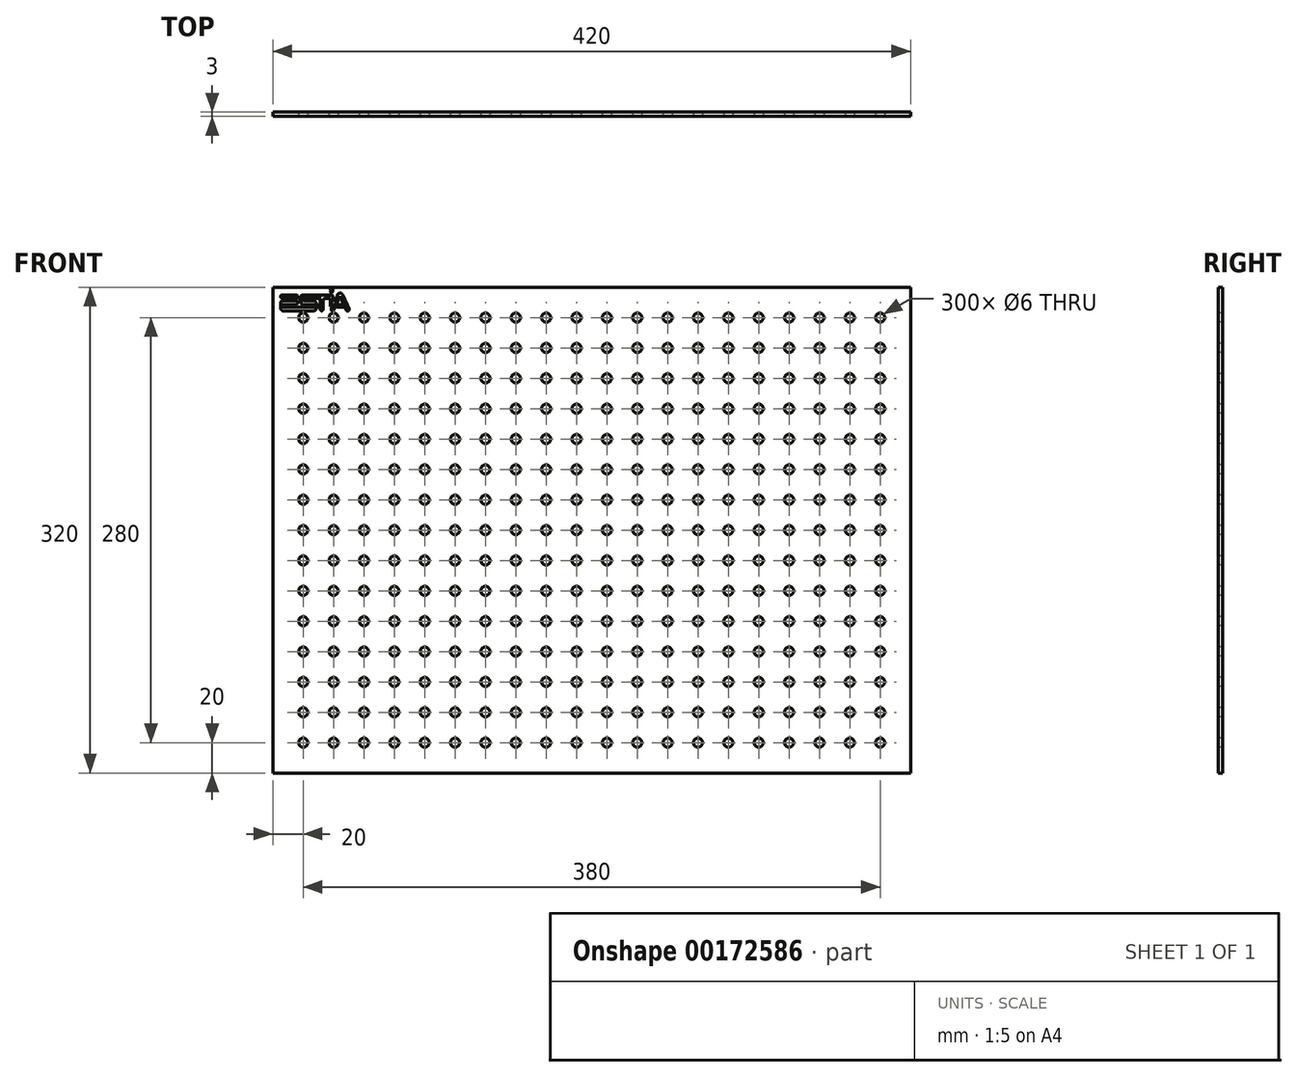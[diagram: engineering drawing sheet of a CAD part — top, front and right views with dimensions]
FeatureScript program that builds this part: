
annotation { "Feature Type Name" : "Feature", "Feature Type Description" : "" }
export const myFeature = defineFeature(function(context is Context, id is Id, definition is map)
    precondition{}
    {
        {
            var Q0;
            Q0=qCreatedBy(makeId("Front.planeOp"),FACE);
            var sketch = newSketch(context, id + "F0", { "sketchPlane" : qUnion([Q0])});
            skLineSegment(sketch, "E0.bottom", {"start": v(0, 0) * mm, "end": v(420, 0) * mm});
            skLineSegment(sketch, "E0.top", {"start": v(0, 320) * mm, "end": v(420, 320) * mm});
            skLineSegment(sketch, "E0.left", {"start": v(0, 0) * mm, "end": v(0, 320) * mm});
            skLineSegment(sketch, "E0.right", {"start": v(420, 0) * mm, "end": v(420, 320) * mm});
            skSolve(sketch);
        }
        {
            var Q0;
            Q0 = qSketchRegion(id + "F0", true);
            extrude(context, id + "F1", {"entities" : qUnion([Q0]), "depth" : 3 * mm});
        }
        {
            var Q0;
            Q0=makeQuery(id+"F1.opExtrude","CAP_FACE",FACE,{"disambiguationData":[OSD([sQuery(id+"F0.wireOp",EDGE,"E0.bottom"),sQuery(id+"F0.wireOp",EDGE,"E0.top"),sQuery(id+"F0.wireOp",EDGE,"E0.left"),sQuery(id+"F0.wireOp",EDGE,"E0.right")])],"isStart":false});
            var sketch = newSketch(context, id + "F2", { "sketchPlane" : qUnion([Q0])});
            skLineSegment(sketch, "E1.0.0", {"start": v(6.34, 307.22) * mm, "end": v(6.34, 308.64) * mm});
            skLineSegment(sketch, "E1.0.1", {"start": v(6.34, 308.64) * mm, "end": v(15.34, 308.64) * mm});
            skLineSegment(sketch, "E1.0.38", {"start": v(15.34, 310.92) * mm, "end": v(6.2, 310.92) * mm});
            skLineSegment(sketch, "E1.0.57", {"start": v(5, 309.72) * mm, "end": v(5, 306.79) * mm});
            skArc(sketch, "E1.0.59", {"start": v(5, 306.79) * mm, "mid": v(5.36, 305.44) * mm, "end": v(6.34, 304.45) * mm});
            skLineSegment(sketch, "E1.0.60", {"start": v(6.34, 304.45) * mm, "end": v(27.4, 304.45) * mm});
            skArc(sketch, "E1.0.61", {"start": v(27.4, 304.45) * mm, "mid": v(29.2, 307.64) * mm, "end": v(27.56, 310.92) * mm});
            skLineSegment(sketch, "E1.0.62", {"start": v(27.56, 310.92) * mm, "end": v(19.38, 310.92) * mm});
            skArc(sketch, "E1.0.63", {"start": v(19.38, 310.92) * mm, "mid": v(19.06, 311.83) * mm, "end": v(19.4, 312.71) * mm});
            skLineSegment(sketch, "E1.0.64", {"start": v(19.4, 312.71) * mm, "end": v(31.79, 312.71) * mm});
            skArc(sketch, "E1.0.65", {"start": v(31.79, 312.71) * mm, "mid": v(31.41, 311.84) * mm, "end": v(31.29, 310.9) * mm});
            skLineSegment(sketch, "E1.0.66", {"start": v(31.29, 310.9) * mm, "end": v(31.29, 305.3) * mm});
            skArc(sketch, "E1.0.67", {"start": v(31.29, 305.3) * mm, "mid": v(32.15, 304.44) * mm, "end": v(33.01, 305.3) * mm});
            skLineSegment(sketch, "E1.0.68", {"start": v(33.01, 305.3) * mm, "end": v(33.01, 310.9) * mm});
            skArc(sketch, "E1.0.69", {"start": v(33.01, 310.9) * mm, "mid": v(33.54, 312.18) * mm, "end": v(34.82, 312.71) * mm});
            skLineSegment(sketch, "E1.0.70", {"start": v(34.82, 312.71) * mm, "end": v(37.81, 312.71) * mm});
            skLineSegment(sketch, "E1.0.71", {"start": v(37.81, 312.71) * mm, "end": v(37.81, 308.44) * mm});
            skArc(sketch, "E1.0.72", {"start": v(37.81, 308.44) * mm, "mid": v(37.92, 307.8) * mm, "end": v(38.22, 307.23) * mm});
            skLineSegment(sketch, "E1.0.73", {"start": v(38.22, 307.23) * mm, "end": v(39.53, 310.23) * mm});
            skLineSegment(sketch, "E1.0.74", {"start": v(39.53, 310.23) * mm, "end": v(39.53, 314.05) * mm});
            skArc(sketch, "E1.0.75", {"start": v(39.53, 314.05) * mm, "mid": v(39.25, 314.72) * mm, "end": v(38.58, 315) * mm});
            skLineSegment(sketch, "E1.0.76", {"start": v(38.58, 315) * mm, "end": v(19.43, 315) * mm});
            skArc(sketch, "E1.0.77", {"start": v(19.43, 315) * mm, "mid": v(17.77, 311.83) * mm, "end": v(19.38, 308.64) * mm});
            skLineSegment(sketch, "E1.0.78", {"start": v(19.38, 308.64) * mm, "end": v(27.56, 308.64) * mm});
            skArc(sketch, "E1.0.79", {"start": v(27.56, 308.64) * mm, "mid": v(28, 307.74) * mm, "end": v(27.56, 306.84) * mm});
            skLineSegment(sketch, "E1.0.80", {"start": v(27.56, 306.84) * mm, "end": v(6.72, 306.84) * mm});
            skArc(sketch, "E1.0.81", {"start": v(6.72, 306.84) * mm, "mid": v(6.45, 306.95) * mm, "end": v(6.34, 307.22) * mm});
            skLineSegment(sketch, "E2.0.2", {"start": v(6.2, 312.71) * mm, "end": v(15.34, 312.71) * mm});
            skLineSegment(sketch, "E2.0.39", {"start": v(15.34, 315) * mm, "end": v(6.2, 315) * mm});
            skLineSegment(sketch, "E3.0.0", {"start": v(44.28, 314.22) * mm, "end": v(48.34, 304.91) * mm});
            skArc(sketch, "E3.0.1", {"start": v(48.34, 304.91) * mm, "mid": v(49.63, 304.4) * mm, "end": v(50.13, 305.7) * mm});
            skLineSegment(sketch, "E3.0.2", {"start": v(50.13, 305.7) * mm, "end": v(46.06, 315) * mm});
            skArc(sketch, "E3.0.3", {"start": v(46.06, 315) * mm, "mid": v(44.28, 316.17) * mm, "end": v(42.49, 315) * mm});
            skLineSegment(sketch, "E3.0.4", {"start": v(42.49, 315) * mm, "end": v(38.42, 305.7) * mm});
            skArc(sketch, "E3.0.5", {"start": v(38.42, 305.7) * mm, "mid": v(38.92, 304.4) * mm, "end": v(40.2, 304.91) * mm});
            skLineSegment(sketch, "E3.0.6", {"start": v(40.2, 304.91) * mm, "end": v(44.28, 314.22) * mm});
            skLineSegment(sketch, "E4.0.2", {"start": v(42.78, 306.84) * mm, "end": v(45.78, 306.84) * mm});
            skLineSegment(sketch, "E4.0.39", {"start": v(45.78, 308.64) * mm, "end": v(42.78, 308.64) * mm});
            skLineSegment(sketch, "E5", {"start": v(32.15, 305.3) * mm, "end": v(49.24, 305.3) * mm, "construction": true});
            skLineSegment(sketch, "E6", {"start": v(26.84, 307.74) * mm, "end": v(8.07, 307.74) * mm, "construction": true});
            skLineSegment(sketch, "E7", {"start": v(7.84, 311.8) * mm, "end": v(20.44, 311.8) * mm, "construction": true});
            skArc(sketch, "E8", {"start": v(6.2, 315) * mm, "mid": v(5.06, 313.86) * mm, "end": v(6.2, 312.71) * mm});
            skArc(sketch, "E9", {"start": v(15.34, 312.71) * mm, "mid": v(16.48, 313.86) * mm, "end": v(15.34, 315) * mm});
            skArc(sketch, "E10", {"start": v(15.34, 308.64) * mm, "mid": v(16.48, 309.78) * mm, "end": v(15.34, 310.92) * mm});
            skArc(sketch, "E11", {"start": v(6.2, 310.92) * mm, "mid": v(5.35, 310.57) * mm, "end": v(5, 309.72) * mm});
            skArc(sketch, "E12", {"start": v(45.78, 306.84) * mm, "mid": v(46.67, 307.74) * mm, "end": v(45.78, 308.64) * mm});
            skArc(sketch, "E13", {"start": v(42.78, 308.64) * mm, "mid": v(41.88, 307.74) * mm, "end": v(42.78, 306.84) * mm});
            skLineSegment(sketch, "E14", {"start": v(42.78, 307.74) * mm, "end": v(45.78, 307.74) * mm, "construction": true});
            skLineSegment(sketch, "E15", {"start": v(44.28, 301.39) * mm, "end": v(44.28, 307.74) * mm, "construction": true});
            skEllipse(sketch, "E16", {"center": v(38.58, 317.9) * mm, "majorRadius": 1.33 * mm, "minorRadius": 0.9 * mm, "majorAxis": v(0, 1)});
            skLineSegment(sketch, "E17", {"start": v(38.58, 310.9) * mm, "end": v(38.58, 315) * mm, "construction": true});
            skSolve(sketch);
        }
        {
            var Q0;
            Q0=makeQuery(id+"F1.opExtrude","CAP_FACE",FACE,{"disambiguationData":[OSD([sQuery(id+"F0.wireOp",EDGE,"E0.bottom"),sQuery(id+"F0.wireOp",EDGE,"E0.top"),sQuery(id+"F0.wireOp",EDGE,"E0.left"),sQuery(id+"F0.wireOp",EDGE,"E0.right")])],"isStart":false});
            var sketch = newSketch(context, id + "F3", { "sketchPlane" : qUnion([Q0])});
            skCircle(sketch, "E18", {"center": v(20, 300) * mm, "radius": 3 * mm});
            skCircle(sketch, "E19.0.1.0", {"center": v(20, 280) * mm, "radius": 3 * mm});
            skCircle(sketch, "E19.0.2.0", {"center": v(20, 260) * mm, "radius": 3 * mm});
            skCircle(sketch, "E19.0.3.0", {"center": v(20, 240) * mm, "radius": 3 * mm});
            skCircle(sketch, "E19.0.4.0", {"center": v(20, 220) * mm, "radius": 3 * mm});
            skCircle(sketch, "E19.0.5.0", {"center": v(20, 200) * mm, "radius": 3 * mm});
            skCircle(sketch, "E19.0.6.0", {"center": v(20, 180) * mm, "radius": 3 * mm});
            skCircle(sketch, "E19.0.7.0", {"center": v(20, 160) * mm, "radius": 3 * mm});
            skCircle(sketch, "E19.0.8.0", {"center": v(20, 140) * mm, "radius": 3 * mm});
            skCircle(sketch, "E19.0.9.0", {"center": v(20, 120) * mm, "radius": 3 * mm});
            skCircle(sketch, "E19.0.10.0", {"center": v(20, 100) * mm, "radius": 3 * mm});
            skCircle(sketch, "E19.0.11.0", {"center": v(20, 80) * mm, "radius": 3 * mm});
            skCircle(sketch, "E19.0.12.0", {"center": v(20, 60) * mm, "radius": 3 * mm});
            skCircle(sketch, "E19.0.13.0", {"center": v(20, 40) * mm, "radius": 3 * mm});
            skCircle(sketch, "E19.0.14.0", {"center": v(20, 20) * mm, "radius": 3 * mm});
            skCircle(sketch, "E19.1.0.0", {"center": v(40, 300) * mm, "radius": 3 * mm});
            skCircle(sketch, "E19.1.1.0", {"center": v(40, 280) * mm, "radius": 3 * mm});
            skCircle(sketch, "E19.1.2.0", {"center": v(40, 260) * mm, "radius": 3 * mm});
            skCircle(sketch, "E19.1.3.0", {"center": v(40, 240) * mm, "radius": 3 * mm});
            skCircle(sketch, "E19.1.4.0", {"center": v(40, 220) * mm, "radius": 3 * mm});
            skCircle(sketch, "E19.1.5.0", {"center": v(40, 200) * mm, "radius": 3 * mm});
            skCircle(sketch, "E19.1.6.0", {"center": v(40, 180) * mm, "radius": 3 * mm});
            skCircle(sketch, "E19.1.7.0", {"center": v(40, 160) * mm, "radius": 3 * mm});
            skCircle(sketch, "E19.1.8.0", {"center": v(40, 140) * mm, "radius": 3 * mm});
            skCircle(sketch, "E19.1.9.0", {"center": v(40, 120) * mm, "radius": 3 * mm});
            skCircle(sketch, "E19.1.10.0", {"center": v(40, 100) * mm, "radius": 3 * mm});
            skCircle(sketch, "E19.1.11.0", {"center": v(40, 80) * mm, "radius": 3 * mm});
            skCircle(sketch, "E19.1.12.0", {"center": v(40, 60) * mm, "radius": 3 * mm});
            skCircle(sketch, "E19.1.13.0", {"center": v(40, 40) * mm, "radius": 3 * mm});
            skCircle(sketch, "E19.1.14.0", {"center": v(40, 20) * mm, "radius": 3 * mm});
            skCircle(sketch, "E19.2.0.0", {"center": v(60, 300) * mm, "radius": 3 * mm});
            skCircle(sketch, "E19.2.1.0", {"center": v(60, 280) * mm, "radius": 3 * mm});
            skCircle(sketch, "E19.2.2.0", {"center": v(60, 260) * mm, "radius": 3 * mm});
            skCircle(sketch, "E19.2.3.0", {"center": v(60, 240) * mm, "radius": 3 * mm});
            skCircle(sketch, "E19.2.4.0", {"center": v(60, 220) * mm, "radius": 3 * mm});
            skCircle(sketch, "E19.2.5.0", {"center": v(60, 200) * mm, "radius": 3 * mm});
            skCircle(sketch, "E19.2.6.0", {"center": v(60, 180) * mm, "radius": 3 * mm});
            skCircle(sketch, "E19.2.7.0", {"center": v(60, 160) * mm, "radius": 3 * mm});
            skCircle(sketch, "E19.2.8.0", {"center": v(60, 140) * mm, "radius": 3 * mm});
            skCircle(sketch, "E19.2.9.0", {"center": v(60, 120) * mm, "radius": 3 * mm});
            skCircle(sketch, "E19.2.10.0", {"center": v(60, 100) * mm, "radius": 3 * mm});
            skCircle(sketch, "E19.2.11.0", {"center": v(60, 80) * mm, "radius": 3 * mm});
            skCircle(sketch, "E19.2.12.0", {"center": v(60, 60) * mm, "radius": 3 * mm});
            skCircle(sketch, "E19.2.13.0", {"center": v(60, 40) * mm, "radius": 3 * mm});
            skCircle(sketch, "E19.2.14.0", {"center": v(60, 20) * mm, "radius": 3 * mm});
            skCircle(sketch, "E19.3.0.0", {"center": v(80, 300) * mm, "radius": 3 * mm});
            skCircle(sketch, "E19.3.1.0", {"center": v(80, 280) * mm, "radius": 3 * mm});
            skCircle(sketch, "E19.3.2.0", {"center": v(80, 260) * mm, "radius": 3 * mm});
            skCircle(sketch, "E19.3.3.0", {"center": v(80, 240) * mm, "radius": 3 * mm});
            skCircle(sketch, "E19.3.4.0", {"center": v(80, 220) * mm, "radius": 3 * mm});
            skCircle(sketch, "E19.3.5.0", {"center": v(80, 200) * mm, "radius": 3 * mm});
            skCircle(sketch, "E19.3.6.0", {"center": v(80, 180) * mm, "radius": 3 * mm});
            skCircle(sketch, "E19.3.7.0", {"center": v(80, 160) * mm, "radius": 3 * mm});
            skCircle(sketch, "E19.3.8.0", {"center": v(80, 140) * mm, "radius": 3 * mm});
            skCircle(sketch, "E19.3.9.0", {"center": v(80, 120) * mm, "radius": 3 * mm});
            skCircle(sketch, "E19.3.10.0", {"center": v(80, 100) * mm, "radius": 3 * mm});
            skCircle(sketch, "E19.3.11.0", {"center": v(80, 80) * mm, "radius": 3 * mm});
            skCircle(sketch, "E19.3.12.0", {"center": v(80, 60) * mm, "radius": 3 * mm});
            skCircle(sketch, "E19.3.13.0", {"center": v(80, 40) * mm, "radius": 3 * mm});
            skCircle(sketch, "E19.3.14.0", {"center": v(80, 20) * mm, "radius": 3 * mm});
            skCircle(sketch, "E19.4.0.0", {"center": v(100, 300) * mm, "radius": 3 * mm});
            skCircle(sketch, "E19.4.1.0", {"center": v(100, 280) * mm, "radius": 3 * mm});
            skCircle(sketch, "E19.4.2.0", {"center": v(100, 260) * mm, "radius": 3 * mm});
            skCircle(sketch, "E19.4.3.0", {"center": v(100, 240) * mm, "radius": 3 * mm});
            skCircle(sketch, "E19.4.4.0", {"center": v(100, 220) * mm, "radius": 3 * mm});
            skCircle(sketch, "E19.4.5.0", {"center": v(100, 200) * mm, "radius": 3 * mm});
            skCircle(sketch, "E19.4.6.0", {"center": v(100, 180) * mm, "radius": 3 * mm});
            skCircle(sketch, "E19.4.7.0", {"center": v(100, 160) * mm, "radius": 3 * mm});
            skCircle(sketch, "E19.4.8.0", {"center": v(100, 140) * mm, "radius": 3 * mm});
            skCircle(sketch, "E19.4.9.0", {"center": v(100, 120) * mm, "radius": 3 * mm});
            skCircle(sketch, "E19.4.10.0", {"center": v(100, 100) * mm, "radius": 3 * mm});
            skCircle(sketch, "E19.4.11.0", {"center": v(100, 80) * mm, "radius": 3 * mm});
            skCircle(sketch, "E19.4.12.0", {"center": v(100, 60) * mm, "radius": 3 * mm});
            skCircle(sketch, "E19.4.13.0", {"center": v(100, 40) * mm, "radius": 3 * mm});
            skCircle(sketch, "E19.4.14.0", {"center": v(100, 20) * mm, "radius": 3 * mm});
            skCircle(sketch, "E19.5.0.0", {"center": v(120, 300) * mm, "radius": 3 * mm});
            skCircle(sketch, "E19.5.1.0", {"center": v(120, 280) * mm, "radius": 3 * mm});
            skCircle(sketch, "E19.5.2.0", {"center": v(120, 260) * mm, "radius": 3 * mm});
            skCircle(sketch, "E19.5.3.0", {"center": v(120, 240) * mm, "radius": 3 * mm});
            skCircle(sketch, "E19.5.4.0", {"center": v(120, 220) * mm, "radius": 3 * mm});
            skCircle(sketch, "E19.5.5.0", {"center": v(120, 200) * mm, "radius": 3 * mm});
            skCircle(sketch, "E19.5.6.0", {"center": v(120, 180) * mm, "radius": 3 * mm});
            skCircle(sketch, "E19.5.7.0", {"center": v(120, 160) * mm, "radius": 3 * mm});
            skCircle(sketch, "E19.5.8.0", {"center": v(120, 140) * mm, "radius": 3 * mm});
            skCircle(sketch, "E19.5.9.0", {"center": v(120, 120) * mm, "radius": 3 * mm});
            skCircle(sketch, "E19.5.10.0", {"center": v(120, 100) * mm, "radius": 3 * mm});
            skCircle(sketch, "E19.5.11.0", {"center": v(120, 80) * mm, "radius": 3 * mm});
            skCircle(sketch, "E19.5.12.0", {"center": v(120, 60) * mm, "radius": 3 * mm});
            skCircle(sketch, "E19.5.13.0", {"center": v(120, 40) * mm, "radius": 3 * mm});
            skCircle(sketch, "E19.5.14.0", {"center": v(120, 20) * mm, "radius": 3 * mm});
            skCircle(sketch, "E19.6.0.0", {"center": v(140, 300) * mm, "radius": 3 * mm});
            skCircle(sketch, "E19.6.1.0", {"center": v(140, 280) * mm, "radius": 3 * mm});
            skCircle(sketch, "E19.6.2.0", {"center": v(140, 260) * mm, "radius": 3 * mm});
            skCircle(sketch, "E19.6.3.0", {"center": v(140, 240) * mm, "radius": 3 * mm});
            skCircle(sketch, "E19.6.4.0", {"center": v(140, 220) * mm, "radius": 3 * mm});
            skCircle(sketch, "E19.6.5.0", {"center": v(140, 200) * mm, "radius": 3 * mm});
            skCircle(sketch, "E19.6.6.0", {"center": v(140, 180) * mm, "radius": 3 * mm});
            skCircle(sketch, "E19.6.7.0", {"center": v(140, 160) * mm, "radius": 3 * mm});
            skCircle(sketch, "E19.6.8.0", {"center": v(140, 140) * mm, "radius": 3 * mm});
            skCircle(sketch, "E19.6.9.0", {"center": v(140, 120) * mm, "radius": 3 * mm});
            skCircle(sketch, "E19.6.10.0", {"center": v(140, 100) * mm, "radius": 3 * mm});
            skCircle(sketch, "E19.6.11.0", {"center": v(140, 80) * mm, "radius": 3 * mm});
            skCircle(sketch, "E19.6.12.0", {"center": v(140, 60) * mm, "radius": 3 * mm});
            skCircle(sketch, "E19.6.13.0", {"center": v(140, 40) * mm, "radius": 3 * mm});
            skCircle(sketch, "E19.6.14.0", {"center": v(140, 20) * mm, "radius": 3 * mm});
            skCircle(sketch, "E19.7.0.0", {"center": v(160, 300) * mm, "radius": 3 * mm});
            skCircle(sketch, "E19.7.1.0", {"center": v(160, 280) * mm, "radius": 3 * mm});
            skCircle(sketch, "E19.7.2.0", {"center": v(160, 260) * mm, "radius": 3 * mm});
            skCircle(sketch, "E19.7.3.0", {"center": v(160, 240) * mm, "radius": 3 * mm});
            skCircle(sketch, "E19.7.4.0", {"center": v(160, 220) * mm, "radius": 3 * mm});
            skCircle(sketch, "E19.7.5.0", {"center": v(160, 200) * mm, "radius": 3 * mm});
            skCircle(sketch, "E19.7.6.0", {"center": v(160, 180) * mm, "radius": 3 * mm});
            skCircle(sketch, "E19.7.7.0", {"center": v(160, 160) * mm, "radius": 3 * mm});
            skCircle(sketch, "E19.7.8.0", {"center": v(160, 140) * mm, "radius": 3 * mm});
            skCircle(sketch, "E19.7.9.0", {"center": v(160, 120) * mm, "radius": 3 * mm});
            skCircle(sketch, "E19.7.10.0", {"center": v(160, 100) * mm, "radius": 3 * mm});
            skCircle(sketch, "E19.7.11.0", {"center": v(160, 80) * mm, "radius": 3 * mm});
            skCircle(sketch, "E19.7.12.0", {"center": v(160, 60) * mm, "radius": 3 * mm});
            skCircle(sketch, "E19.7.13.0", {"center": v(160, 40) * mm, "radius": 3 * mm});
            skCircle(sketch, "E19.7.14.0", {"center": v(160, 20) * mm, "radius": 3 * mm});
            skCircle(sketch, "E19.8.0.0", {"center": v(180, 300) * mm, "radius": 3 * mm});
            skCircle(sketch, "E19.8.1.0", {"center": v(180, 280) * mm, "radius": 3 * mm});
            skCircle(sketch, "E19.8.2.0", {"center": v(180, 260) * mm, "radius": 3 * mm});
            skCircle(sketch, "E19.8.3.0", {"center": v(180, 240) * mm, "radius": 3 * mm});
            skCircle(sketch, "E19.8.4.0", {"center": v(180, 220) * mm, "radius": 3 * mm});
            skCircle(sketch, "E19.8.5.0", {"center": v(180, 200) * mm, "radius": 3 * mm});
            skCircle(sketch, "E19.8.6.0", {"center": v(180, 180) * mm, "radius": 3 * mm});
            skCircle(sketch, "E19.8.7.0", {"center": v(180, 160) * mm, "radius": 3 * mm});
            skCircle(sketch, "E19.8.8.0", {"center": v(180, 140) * mm, "radius": 3 * mm});
            skCircle(sketch, "E19.8.9.0", {"center": v(180, 120) * mm, "radius": 3 * mm});
            skCircle(sketch, "E19.8.10.0", {"center": v(180, 100) * mm, "radius": 3 * mm});
            skCircle(sketch, "E19.8.11.0", {"center": v(180, 80) * mm, "radius": 3 * mm});
            skCircle(sketch, "E19.8.12.0", {"center": v(180, 60) * mm, "radius": 3 * mm});
            skCircle(sketch, "E19.8.13.0", {"center": v(180, 40) * mm, "radius": 3 * mm});
            skCircle(sketch, "E19.8.14.0", {"center": v(180, 20) * mm, "radius": 3 * mm});
            skCircle(sketch, "E19.9.0.0", {"center": v(200, 300) * mm, "radius": 3 * mm});
            skCircle(sketch, "E19.9.1.0", {"center": v(200, 280) * mm, "radius": 3 * mm});
            skCircle(sketch, "E19.9.2.0", {"center": v(200, 260) * mm, "radius": 3 * mm});
            skCircle(sketch, "E19.9.3.0", {"center": v(200, 240) * mm, "radius": 3 * mm});
            skCircle(sketch, "E19.9.4.0", {"center": v(200, 220) * mm, "radius": 3 * mm});
            skCircle(sketch, "E19.9.5.0", {"center": v(200, 200) * mm, "radius": 3 * mm});
            skCircle(sketch, "E19.9.6.0", {"center": v(200, 180) * mm, "radius": 3 * mm});
            skCircle(sketch, "E19.9.7.0", {"center": v(200, 160) * mm, "radius": 3 * mm});
            skCircle(sketch, "E19.9.8.0", {"center": v(200, 140) * mm, "radius": 3 * mm});
            skCircle(sketch, "E19.9.9.0", {"center": v(200, 120) * mm, "radius": 3 * mm});
            skCircle(sketch, "E19.9.10.0", {"center": v(200, 100) * mm, "radius": 3 * mm});
            skCircle(sketch, "E19.9.11.0", {"center": v(200, 80) * mm, "radius": 3 * mm});
            skCircle(sketch, "E19.9.12.0", {"center": v(200, 60) * mm, "radius": 3 * mm});
            skCircle(sketch, "E19.9.13.0", {"center": v(200, 40) * mm, "radius": 3 * mm});
            skCircle(sketch, "E19.9.14.0", {"center": v(200, 20) * mm, "radius": 3 * mm});
            skCircle(sketch, "E19.10.0.0", {"center": v(220, 300) * mm, "radius": 3 * mm});
            skCircle(sketch, "E19.10.1.0", {"center": v(220, 280) * mm, "radius": 3 * mm});
            skCircle(sketch, "E19.10.2.0", {"center": v(220, 260) * mm, "radius": 3 * mm});
            skCircle(sketch, "E19.10.3.0", {"center": v(220, 240) * mm, "radius": 3 * mm});
            skCircle(sketch, "E19.10.4.0", {"center": v(220, 220) * mm, "radius": 3 * mm});
            skCircle(sketch, "E19.10.5.0", {"center": v(220, 200) * mm, "radius": 3 * mm});
            skCircle(sketch, "E19.10.6.0", {"center": v(220, 180) * mm, "radius": 3 * mm});
            skCircle(sketch, "E19.10.7.0", {"center": v(220, 160) * mm, "radius": 3 * mm});
            skCircle(sketch, "E19.10.8.0", {"center": v(220, 140) * mm, "radius": 3 * mm});
            skCircle(sketch, "E19.10.9.0", {"center": v(220, 120) * mm, "radius": 3 * mm});
            skCircle(sketch, "E19.10.10.0", {"center": v(220, 100) * mm, "radius": 3 * mm});
            skCircle(sketch, "E19.10.11.0", {"center": v(220, 80) * mm, "radius": 3 * mm});
            skCircle(sketch, "E19.10.12.0", {"center": v(220, 60) * mm, "radius": 3 * mm});
            skCircle(sketch, "E19.10.13.0", {"center": v(220, 40) * mm, "radius": 3 * mm});
            skCircle(sketch, "E19.10.14.0", {"center": v(220, 20) * mm, "radius": 3 * mm});
            skCircle(sketch, "E19.11.0.0", {"center": v(240, 300) * mm, "radius": 3 * mm});
            skCircle(sketch, "E19.11.1.0", {"center": v(240, 280) * mm, "radius": 3 * mm});
            skCircle(sketch, "E19.11.2.0", {"center": v(240, 260) * mm, "radius": 3 * mm});
            skCircle(sketch, "E19.11.3.0", {"center": v(240, 240) * mm, "radius": 3 * mm});
            skCircle(sketch, "E19.11.4.0", {"center": v(240, 220) * mm, "radius": 3 * mm});
            skCircle(sketch, "E19.11.5.0", {"center": v(240, 200) * mm, "radius": 3 * mm});
            skCircle(sketch, "E19.11.6.0", {"center": v(240, 180) * mm, "radius": 3 * mm});
            skCircle(sketch, "E19.11.7.0", {"center": v(240, 160) * mm, "radius": 3 * mm});
            skCircle(sketch, "E19.11.8.0", {"center": v(240, 140) * mm, "radius": 3 * mm});
            skCircle(sketch, "E19.11.9.0", {"center": v(240, 120) * mm, "radius": 3 * mm});
            skCircle(sketch, "E19.11.10.0", {"center": v(240, 100) * mm, "radius": 3 * mm});
            skCircle(sketch, "E19.11.11.0", {"center": v(240, 80) * mm, "radius": 3 * mm});
            skCircle(sketch, "E19.11.12.0", {"center": v(240, 60) * mm, "radius": 3 * mm});
            skCircle(sketch, "E19.11.13.0", {"center": v(240, 40) * mm, "radius": 3 * mm});
            skCircle(sketch, "E19.11.14.0", {"center": v(240, 20) * mm, "radius": 3 * mm});
            skCircle(sketch, "E19.12.0.0", {"center": v(260, 300) * mm, "radius": 3 * mm});
            skCircle(sketch, "E19.12.1.0", {"center": v(260, 280) * mm, "radius": 3 * mm});
            skCircle(sketch, "E19.12.2.0", {"center": v(260, 260) * mm, "radius": 3 * mm});
            skCircle(sketch, "E19.12.3.0", {"center": v(260, 240) * mm, "radius": 3 * mm});
            skCircle(sketch, "E19.12.4.0", {"center": v(260, 220) * mm, "radius": 3 * mm});
            skCircle(sketch, "E19.12.5.0", {"center": v(260, 200) * mm, "radius": 3 * mm});
            skCircle(sketch, "E19.12.6.0", {"center": v(260, 180) * mm, "radius": 3 * mm});
            skCircle(sketch, "E19.12.7.0", {"center": v(260, 160) * mm, "radius": 3 * mm});
            skCircle(sketch, "E19.12.8.0", {"center": v(260, 140) * mm, "radius": 3 * mm});
            skCircle(sketch, "E19.12.9.0", {"center": v(260, 120) * mm, "radius": 3 * mm});
            skCircle(sketch, "E19.12.10.0", {"center": v(260, 100) * mm, "radius": 3 * mm});
            skCircle(sketch, "E19.12.11.0", {"center": v(260, 80) * mm, "radius": 3 * mm});
            skCircle(sketch, "E19.12.12.0", {"center": v(260, 60) * mm, "radius": 3 * mm});
            skCircle(sketch, "E19.12.13.0", {"center": v(260, 40) * mm, "radius": 3 * mm});
            skCircle(sketch, "E19.12.14.0", {"center": v(260, 20) * mm, "radius": 3 * mm});
            skCircle(sketch, "E19.13.0.0", {"center": v(280, 300) * mm, "radius": 3 * mm});
            skCircle(sketch, "E19.13.1.0", {"center": v(280, 280) * mm, "radius": 3 * mm});
            skCircle(sketch, "E19.13.2.0", {"center": v(280, 260) * mm, "radius": 3 * mm});
            skCircle(sketch, "E19.13.3.0", {"center": v(280, 240) * mm, "radius": 3 * mm});
            skCircle(sketch, "E19.13.4.0", {"center": v(280, 220) * mm, "radius": 3 * mm});
            skCircle(sketch, "E19.13.5.0", {"center": v(280, 200) * mm, "radius": 3 * mm});
            skCircle(sketch, "E19.13.6.0", {"center": v(280, 180) * mm, "radius": 3 * mm});
            skCircle(sketch, "E19.13.7.0", {"center": v(280, 160) * mm, "radius": 3 * mm});
            skCircle(sketch, "E19.13.8.0", {"center": v(280, 140) * mm, "radius": 3 * mm});
            skCircle(sketch, "E19.13.9.0", {"center": v(280, 120) * mm, "radius": 3 * mm});
            skCircle(sketch, "E19.13.10.0", {"center": v(280, 100) * mm, "radius": 3 * mm});
            skCircle(sketch, "E19.13.11.0", {"center": v(280, 80) * mm, "radius": 3 * mm});
            skCircle(sketch, "E19.13.12.0", {"center": v(280, 60) * mm, "radius": 3 * mm});
            skCircle(sketch, "E19.13.13.0", {"center": v(280, 40) * mm, "radius": 3 * mm});
            skCircle(sketch, "E19.13.14.0", {"center": v(280, 20) * mm, "radius": 3 * mm});
            skCircle(sketch, "E19.14.0.0", {"center": v(300, 300) * mm, "radius": 3 * mm});
            skCircle(sketch, "E19.14.1.0", {"center": v(300, 280) * mm, "radius": 3 * mm});
            skCircle(sketch, "E19.14.2.0", {"center": v(300, 260) * mm, "radius": 3 * mm});
            skCircle(sketch, "E19.14.3.0", {"center": v(300, 240) * mm, "radius": 3 * mm});
            skCircle(sketch, "E19.14.4.0", {"center": v(300, 220) * mm, "radius": 3 * mm});
            skCircle(sketch, "E19.14.5.0", {"center": v(300, 200) * mm, "radius": 3 * mm});
            skCircle(sketch, "E19.14.6.0", {"center": v(300, 180) * mm, "radius": 3 * mm});
            skCircle(sketch, "E19.14.7.0", {"center": v(300, 160) * mm, "radius": 3 * mm});
            skCircle(sketch, "E19.14.8.0", {"center": v(300, 140) * mm, "radius": 3 * mm});
            skCircle(sketch, "E19.14.9.0", {"center": v(300, 120) * mm, "radius": 3 * mm});
            skCircle(sketch, "E19.14.10.0", {"center": v(300, 100) * mm, "radius": 3 * mm});
            skCircle(sketch, "E19.14.11.0", {"center": v(300, 80) * mm, "radius": 3 * mm});
            skCircle(sketch, "E19.14.12.0", {"center": v(300, 60) * mm, "radius": 3 * mm});
            skCircle(sketch, "E19.14.13.0", {"center": v(300, 40) * mm, "radius": 3 * mm});
            skCircle(sketch, "E19.14.14.0", {"center": v(300, 20) * mm, "radius": 3 * mm});
            skCircle(sketch, "E19.15.0.0", {"center": v(320, 300) * mm, "radius": 3 * mm});
            skCircle(sketch, "E19.15.1.0", {"center": v(320, 280) * mm, "radius": 3 * mm});
            skCircle(sketch, "E19.15.2.0", {"center": v(320, 260) * mm, "radius": 3 * mm});
            skCircle(sketch, "E19.15.3.0", {"center": v(320, 240) * mm, "radius": 3 * mm});
            skCircle(sketch, "E19.15.4.0", {"center": v(320, 220) * mm, "radius": 3 * mm});
            skCircle(sketch, "E19.15.5.0", {"center": v(320, 200) * mm, "radius": 3 * mm});
            skCircle(sketch, "E19.15.6.0", {"center": v(320, 180) * mm, "radius": 3 * mm});
            skCircle(sketch, "E19.15.7.0", {"center": v(320, 160) * mm, "radius": 3 * mm});
            skCircle(sketch, "E19.15.8.0", {"center": v(320, 140) * mm, "radius": 3 * mm});
            skCircle(sketch, "E19.15.9.0", {"center": v(320, 120) * mm, "radius": 3 * mm});
            skCircle(sketch, "E19.15.10.0", {"center": v(320, 100) * mm, "radius": 3 * mm});
            skCircle(sketch, "E19.15.11.0", {"center": v(320, 80) * mm, "radius": 3 * mm});
            skCircle(sketch, "E19.15.12.0", {"center": v(320, 60) * mm, "radius": 3 * mm});
            skCircle(sketch, "E19.15.13.0", {"center": v(320, 40) * mm, "radius": 3 * mm});
            skCircle(sketch, "E19.15.14.0", {"center": v(320, 20) * mm, "radius": 3 * mm});
            skCircle(sketch, "E19.16.0.0", {"center": v(340, 300) * mm, "radius": 3 * mm});
            skCircle(sketch, "E19.16.1.0", {"center": v(340, 280) * mm, "radius": 3 * mm});
            skCircle(sketch, "E19.16.2.0", {"center": v(340, 260) * mm, "radius": 3 * mm});
            skCircle(sketch, "E19.16.3.0", {"center": v(340, 240) * mm, "radius": 3 * mm});
            skCircle(sketch, "E19.16.4.0", {"center": v(340, 220) * mm, "radius": 3 * mm});
            skCircle(sketch, "E19.16.5.0", {"center": v(340, 200) * mm, "radius": 3 * mm});
            skCircle(sketch, "E19.16.6.0", {"center": v(340, 180) * mm, "radius": 3 * mm});
            skCircle(sketch, "E19.16.7.0", {"center": v(340, 160) * mm, "radius": 3 * mm});
            skCircle(sketch, "E19.16.8.0", {"center": v(340, 140) * mm, "radius": 3 * mm});
            skCircle(sketch, "E19.16.9.0", {"center": v(340, 120) * mm, "radius": 3 * mm});
            skCircle(sketch, "E19.16.10.0", {"center": v(340, 100) * mm, "radius": 3 * mm});
            skCircle(sketch, "E19.16.11.0", {"center": v(340, 80) * mm, "radius": 3 * mm});
            skCircle(sketch, "E19.16.12.0", {"center": v(340, 60) * mm, "radius": 3 * mm});
            skCircle(sketch, "E19.16.13.0", {"center": v(340, 40) * mm, "radius": 3 * mm});
            skCircle(sketch, "E19.16.14.0", {"center": v(340, 20) * mm, "radius": 3 * mm});
            skCircle(sketch, "E19.17.0.0", {"center": v(360, 300) * mm, "radius": 3 * mm});
            skCircle(sketch, "E19.17.1.0", {"center": v(360, 280) * mm, "radius": 3 * mm});
            skCircle(sketch, "E19.17.2.0", {"center": v(360, 260) * mm, "radius": 3 * mm});
            skCircle(sketch, "E19.17.3.0", {"center": v(360, 240) * mm, "radius": 3 * mm});
            skCircle(sketch, "E19.17.4.0", {"center": v(360, 220) * mm, "radius": 3 * mm});
            skCircle(sketch, "E19.17.5.0", {"center": v(360, 200) * mm, "radius": 3 * mm});
            skCircle(sketch, "E19.17.6.0", {"center": v(360, 180) * mm, "radius": 3 * mm});
            skCircle(sketch, "E19.17.7.0", {"center": v(360, 160) * mm, "radius": 3 * mm});
            skCircle(sketch, "E19.17.8.0", {"center": v(360, 140) * mm, "radius": 3 * mm});
            skCircle(sketch, "E19.17.9.0", {"center": v(360, 120) * mm, "radius": 3 * mm});
            skCircle(sketch, "E19.17.10.0", {"center": v(360, 100) * mm, "radius": 3 * mm});
            skCircle(sketch, "E19.17.11.0", {"center": v(360, 80) * mm, "radius": 3 * mm});
            skCircle(sketch, "E19.17.12.0", {"center": v(360, 60) * mm, "radius": 3 * mm});
            skCircle(sketch, "E19.17.13.0", {"center": v(360, 40) * mm, "radius": 3 * mm});
            skCircle(sketch, "E19.17.14.0", {"center": v(360, 20) * mm, "radius": 3 * mm});
            skCircle(sketch, "E19.18.0.0", {"center": v(380, 300) * mm, "radius": 3 * mm});
            skCircle(sketch, "E19.18.1.0", {"center": v(380, 280) * mm, "radius": 3 * mm});
            skCircle(sketch, "E19.18.2.0", {"center": v(380, 260) * mm, "radius": 3 * mm});
            skCircle(sketch, "E19.18.3.0", {"center": v(380, 240) * mm, "radius": 3 * mm});
            skCircle(sketch, "E19.18.4.0", {"center": v(380, 220) * mm, "radius": 3 * mm});
            skCircle(sketch, "E19.18.5.0", {"center": v(380, 200) * mm, "radius": 3 * mm});
            skCircle(sketch, "E19.18.6.0", {"center": v(380, 180) * mm, "radius": 3 * mm});
            skCircle(sketch, "E19.18.7.0", {"center": v(380, 160) * mm, "radius": 3 * mm});
            skCircle(sketch, "E19.18.8.0", {"center": v(380, 140) * mm, "radius": 3 * mm});
            skCircle(sketch, "E19.18.9.0", {"center": v(380, 120) * mm, "radius": 3 * mm});
            skCircle(sketch, "E19.18.10.0", {"center": v(380, 100) * mm, "radius": 3 * mm});
            skCircle(sketch, "E19.18.11.0", {"center": v(380, 80) * mm, "radius": 3 * mm});
            skCircle(sketch, "E19.18.12.0", {"center": v(380, 60) * mm, "radius": 3 * mm});
            skCircle(sketch, "E19.18.13.0", {"center": v(380, 40) * mm, "radius": 3 * mm});
            skCircle(sketch, "E19.18.14.0", {"center": v(380, 20) * mm, "radius": 3 * mm});
            skCircle(sketch, "E19.19.0.0", {"center": v(400, 300) * mm, "radius": 3 * mm});
            skCircle(sketch, "E19.19.1.0", {"center": v(400, 280) * mm, "radius": 3 * mm});
            skCircle(sketch, "E19.19.2.0", {"center": v(400, 260) * mm, "radius": 3 * mm});
            skCircle(sketch, "E19.19.3.0", {"center": v(400, 240) * mm, "radius": 3 * mm});
            skCircle(sketch, "E19.19.4.0", {"center": v(400, 220) * mm, "radius": 3 * mm});
            skCircle(sketch, "E19.19.5.0", {"center": v(400, 200) * mm, "radius": 3 * mm});
            skCircle(sketch, "E19.19.6.0", {"center": v(400, 180) * mm, "radius": 3 * mm});
            skCircle(sketch, "E19.19.7.0", {"center": v(400, 160) * mm, "radius": 3 * mm});
            skCircle(sketch, "E19.19.8.0", {"center": v(400, 140) * mm, "radius": 3 * mm});
            skCircle(sketch, "E19.19.9.0", {"center": v(400, 120) * mm, "radius": 3 * mm});
            skCircle(sketch, "E19.19.10.0", {"center": v(400, 100) * mm, "radius": 3 * mm});
            skCircle(sketch, "E19.19.11.0", {"center": v(400, 80) * mm, "radius": 3 * mm});
            skCircle(sketch, "E19.19.12.0", {"center": v(400, 60) * mm, "radius": 3 * mm});
            skCircle(sketch, "E19.19.13.0", {"center": v(400, 40) * mm, "radius": 3 * mm});
            skCircle(sketch, "E19.19.14.0", {"center": v(400, 20) * mm, "radius": 3 * mm});
            skLineSegment(sketch, "E19.direction1", {"start": v(20, 300) * mm, "end": v(40, 300) * mm, "construction": true});
            skLineSegment(sketch, "E19.direction2", {"start": v(20, 300) * mm, "end": v(20, 280) * mm, "construction": true});
            skSolve(sketch);
        }
        {
            var Q0;
            Q0 = qSketchRegion(id + "F3", true);
            extrude(context, id + "F4", {"entities" : qUnion([Q0]), "operationType" : NewBodyOperationType.REMOVE, "oppositeDirection" : true, "depth" : 25 * mm});
        }
        {
            var Q0;
            Q0 = qSketchRegion(id + "F2", true);
            extrude(context, id + "F5", {"entities" : qUnion([Q0]), "operationType" : NewBodyOperationType.REMOVE, "oppositeDirection" : true, "depth" : 0.5 * mm, "offsetDistance" : 25 * mm});
        }
    });
